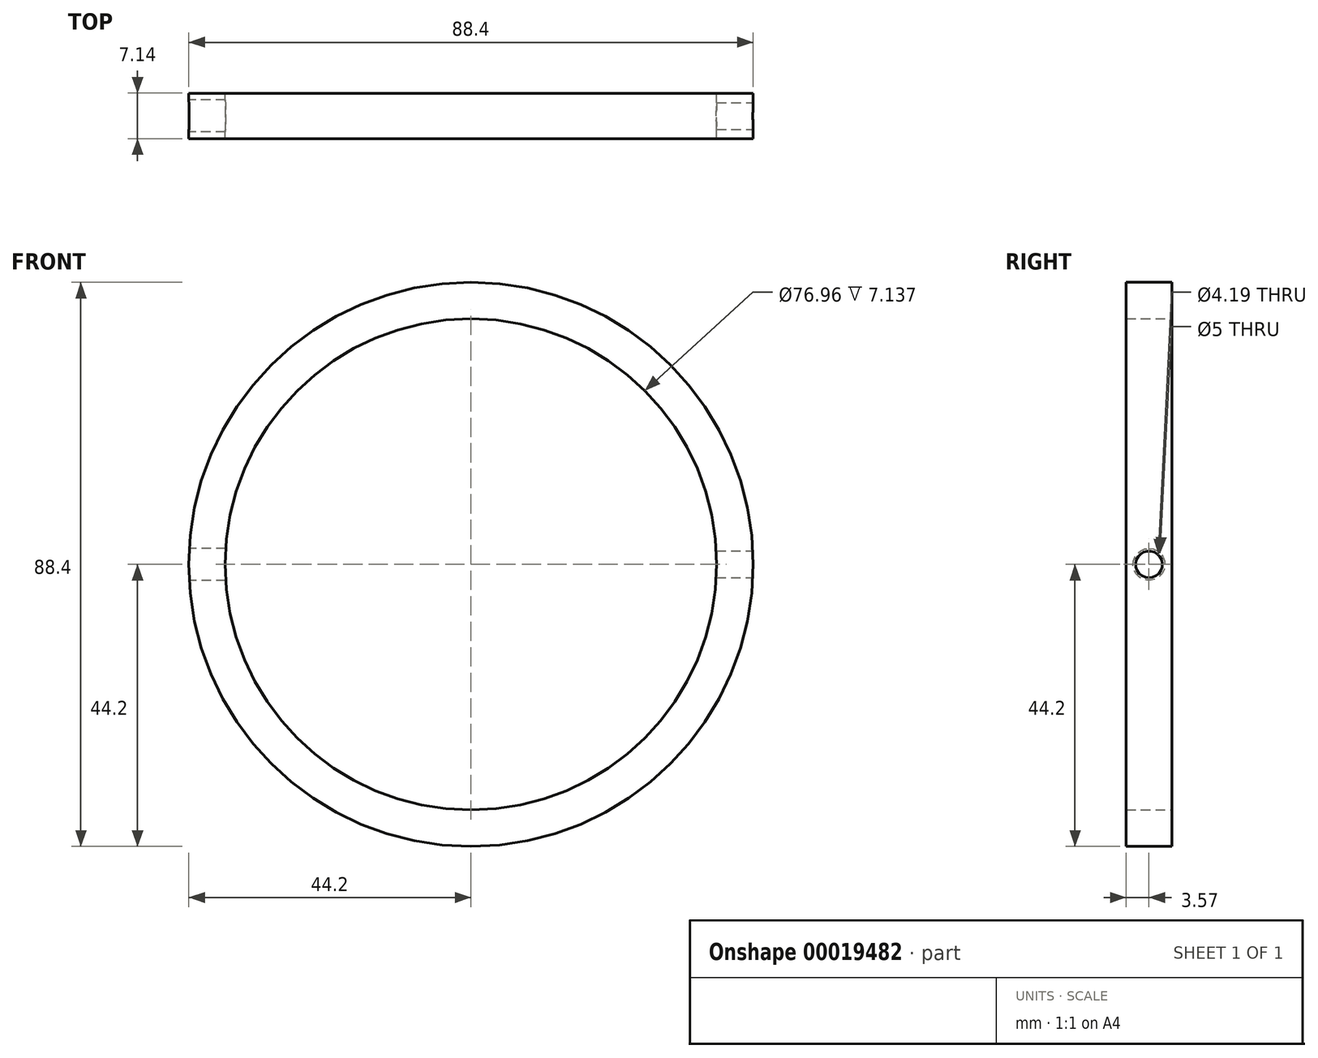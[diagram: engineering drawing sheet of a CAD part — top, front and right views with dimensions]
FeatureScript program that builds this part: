
annotation { "Feature Type Name" : "Feature", "Feature Type Description" : "" }
export const myFeature = defineFeature(function(context is Context, id is Id, definition is map)
    precondition{}
    {
        {
            var Q0;
            Q0=qCreatedBy(makeId("Right.planeOp"),FACE);
            cPlane(context, id + "F0", {"entities" : qUnion([Q0]), "cplaneType" : CPlaneType.OFFSET, "offset" : 50.8 * mm, "width" : 152.4 * mm, "height" : 152.4 * mm});
        }
        {
            var Q0;
            Q0=qCreatedBy(makeId("Front.planeOp"),FACE);
            var sketch = newSketch(context, id + "F1", { "sketchPlane" : qUnion([Q0])});
            skCircle(sketch, "E0", {"center": v(0, 0) * mm, "radius": 38.48 * mm});
            skCircle(sketch, "E1", {"center": v(0, 0) * mm, "radius": 44.2 * mm});
            skSolve(sketch);
        }
        {
            var Q0;
            Q0 = qSketchRegion(id + "F1", true);
            extrude(context, id + "F2", {"entities" : qUnion([Q0]), "endBound" : BoundingType.SYMMETRIC, "depth" : 7.14 * mm});
        }
        {
            var Q0;
            Q0=qCreatedBy(id+"F0.planeOp",FACE);
            var sketch = newSketch(context, id + "F3", { "sketchPlane" : qUnion([Q0])});
            skPoint(sketch, "E2", {"position": v(0, 0) * mm});
            skSolve(sketch);
        }
        {
            var Q0;
            Q0=qCreatedBy(makeId("Right.planeOp"),FACE);
            cPlane(context, id + "F4", {"entities" : qUnion([Q0]), "cplaneType" : CPlaneType.OFFSET, "offset" : 50.8 * mm, "oppositeDirection" : true, "width" : 152.4 * mm, "height" : 152.4 * mm});
        }
        {
            var Q0;
            Q0=qCreatedBy(id+"F4.planeOp",FACE);
            var sketch = newSketch(context, id + "F5", { "sketchPlane" : qUnion([Q0])});
            skPoint(sketch, "E3", {"position": v(0, 0) * mm});
            skSolve(sketch);
        }
        {
            var Q0;
            Q0=sQuery(id+"F3.wireOp",VERTEX,"E2");
            var Q1;
            Q1=makeQuery(id+"F2.opExtrude","SWEPT_BODY",BODY,{"disambiguationData":[OSD([sQuery(id+"F1.wireOp",EDGE,"E0"),sQuery(id+"F1.wireOp",EDGE,"E1")])]});
            hole(context, id + "F6", {"style" : HoleStyle.SIMPLE, "holeDiameter" : 4.2 * mm, "endStyle" : HoleEndStyle.BLIND, "holeDepth" : 25.4 * mm, "locations" : qUnion([Q0]), "scope" : qUnion([Q1])});
        }
        {
            var Q0;
            Q0=sQuery(id+"F5.wireOp",VERTEX,"E3");
            var Q1;
            Q1=makeQuery(id+"F2.opExtrude","SWEPT_BODY",BODY,{"disambiguationData":[OSD([sQuery(id+"F1.wireOp",EDGE,"E0"),sQuery(id+"F1.wireOp",EDGE,"E1")])]});
            hole(context, id + "F7", {"style" : HoleStyle.SIMPLE, "holeDiameter" : 5 * mm, "endStyle" : HoleEndStyle.BLIND, "oppositeDirection" : true, "holeDepth" : 25.4 * mm, "locations" : qUnion([Q0]), "scope" : qUnion([Q1])});
        }
    });
